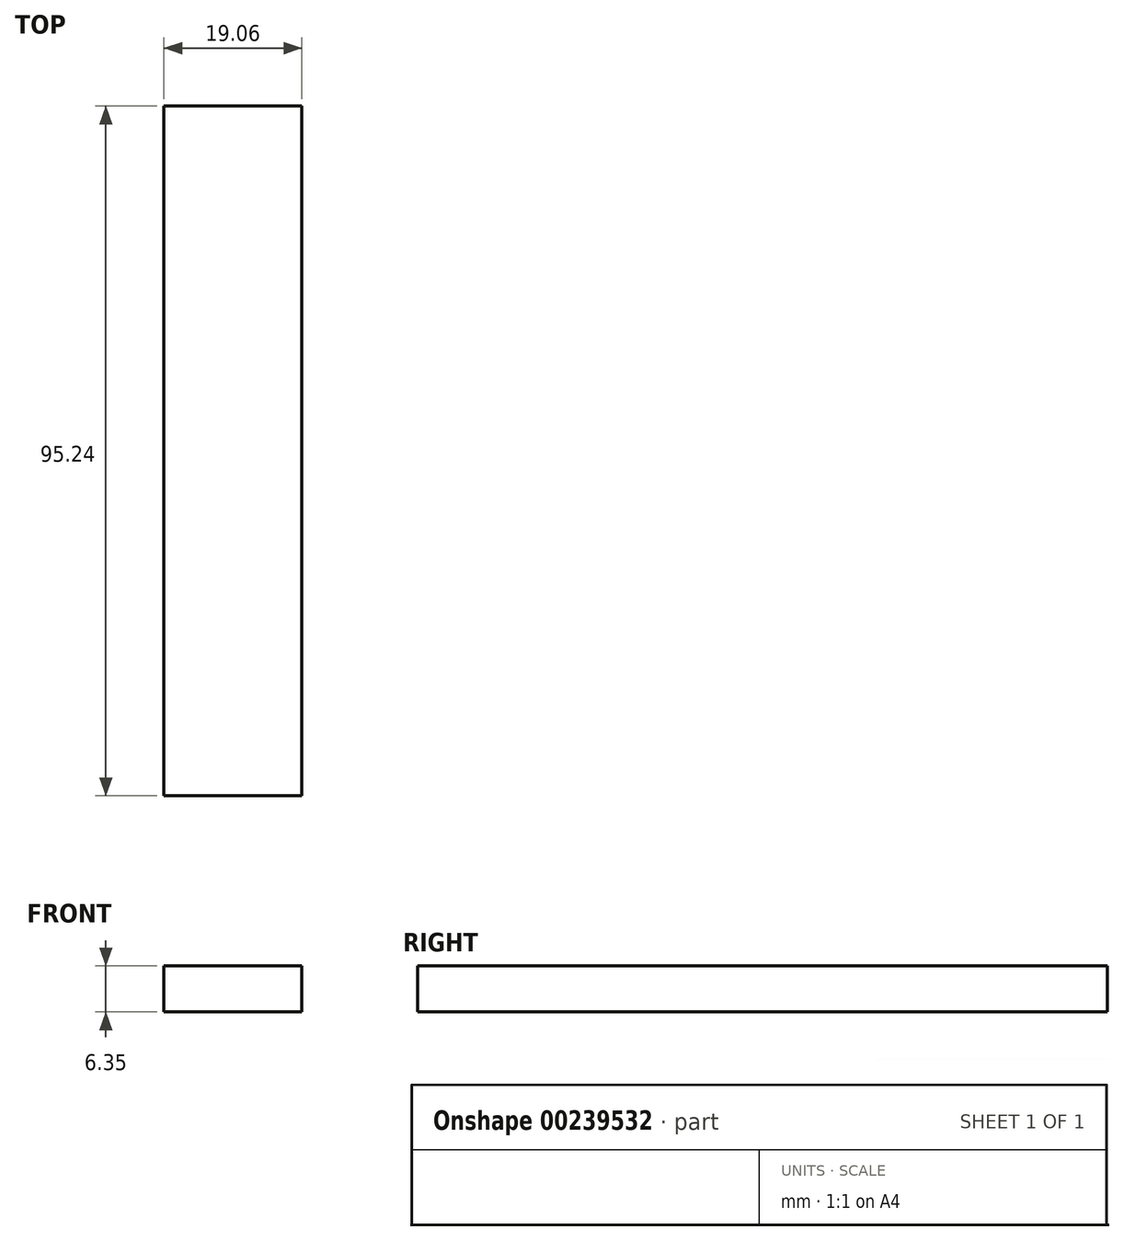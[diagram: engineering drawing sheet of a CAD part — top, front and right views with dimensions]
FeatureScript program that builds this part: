
annotation { "Feature Type Name" : "Feature", "Feature Type Description" : "" }
export const myFeature = defineFeature(function(context is Context, id is Id, definition is map)
    precondition{}
    {
        {
            var Q0;
            Q0=qCreatedBy(makeId("Top.planeOp"),FACE);
            var sketch = newSketch(context, id + "F0", { "sketchPlane" : qUnion([Q0])});
            skLineSegment(sketch, "E0.bottom", {"start": v(9.53, 47.63) * mm, "end": v(-9.53, 47.63) * mm});
            skLineSegment(sketch, "E0.top", {"start": v(9.52, -47.63) * mm, "end": v(-9.53, -47.63) * mm});
            skLineSegment(sketch, "E0.left", {"start": v(9.53, 47.63) * mm, "end": v(9.52, -47.63) * mm});
            skLineSegment(sketch, "E0.right", {"start": v(-9.53, 47.63) * mm, "end": v(-9.53, -47.63) * mm});
            skPoint(sketch, "E0.middle", {"position": v(0, 0) * mm});
            skSolve(sketch);
        }
        {
            var Q0;
            Q0 = qSketchRegion(id + "F0", true);
            extrude(context, id + "F1", {"entities" : qUnion([Q0]), "depth" : 6.35 * mm});
        }
    });
